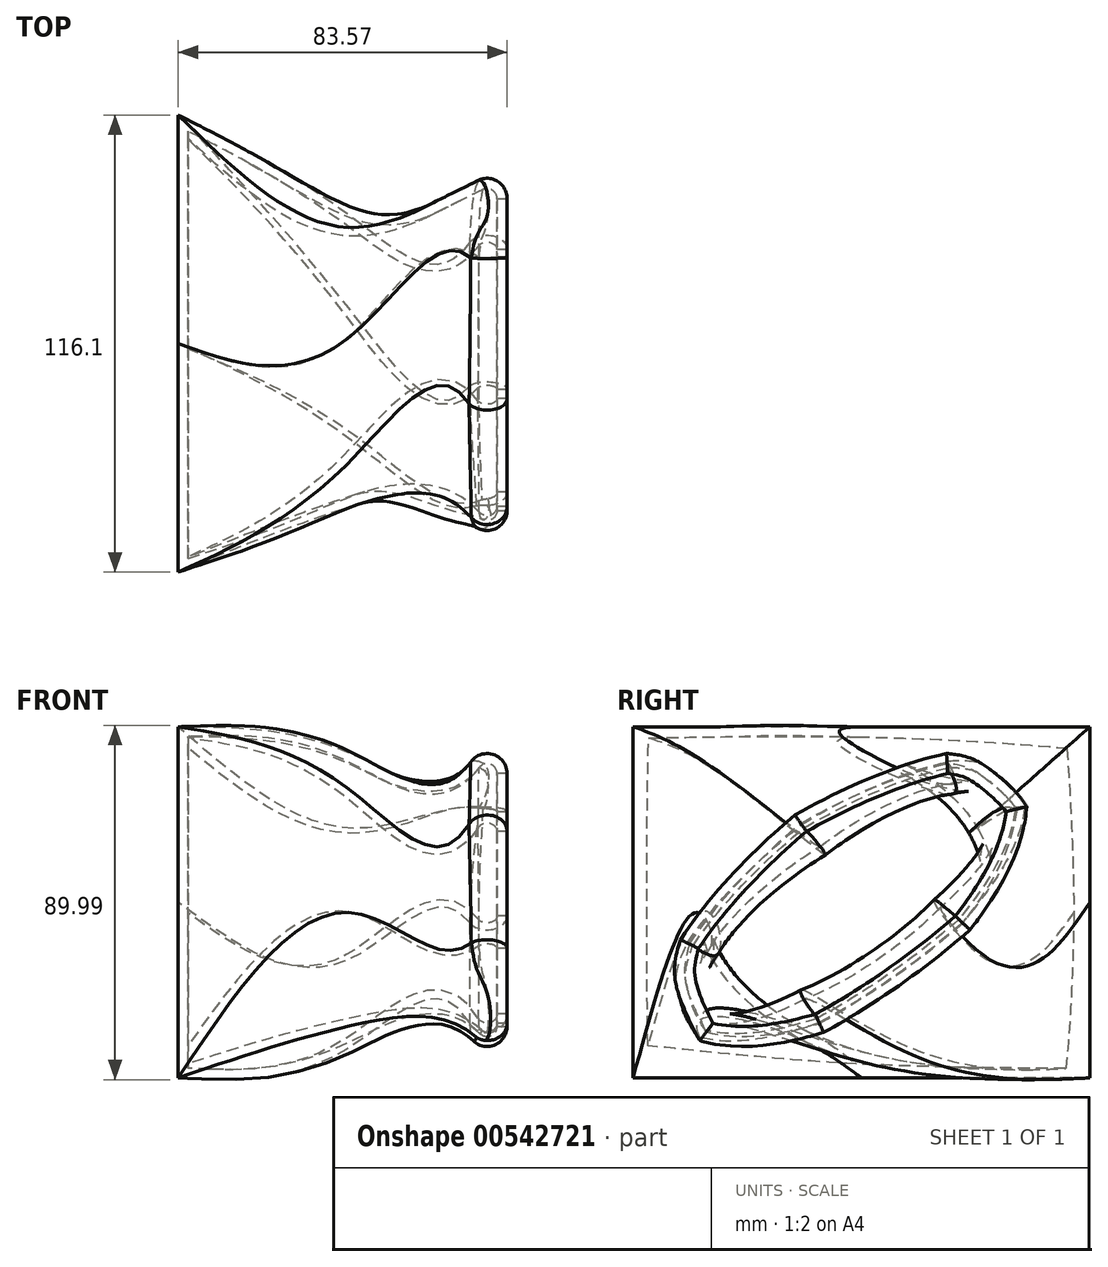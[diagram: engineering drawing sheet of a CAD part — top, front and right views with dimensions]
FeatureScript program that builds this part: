
annotation { "Feature Type Name" : "Feature", "Feature Type Description" : "" }
export const myFeature = defineFeature(function(context is Context, id is Id, definition is map)
    precondition{}
    {
        {
            var Q0;
            Q0=qCreatedBy(makeId("Right.planeOp"),FACE);
            cPlane(context, id + "F0", {"entities" : qUnion([Q0]), "cplaneType" : CPlaneType.OFFSET, "offset" : 25.4 * mm, "width" : 152.4 * mm, "height" : 152.4 * mm});
        }
        {
            var Q0;
            Q0=qCreatedBy(makeId("Right.planeOp"),FACE);
            cPlane(context, id + "F1", {"entities" : qUnion([Q0]), "cplaneType" : CPlaneType.OFFSET, "offset" : 39.12 * mm, "width" : 152.4 * mm, "height" : 152.4 * mm});
        }
        {
            var Q0;
            Q0=qCreatedBy(id+"F1.planeOp",FACE);
            var sketch = newSketch(context, id + "F2", { "sketchPlane" : qUnion([Q0])});
            skCircle(sketch, "E0.cCircle", {"center": v(0, 0) * mm, "radius": 48.41 * mm, "construction": true});
            skLineSegment(sketch, "E0.0", {"start": v(48.41, 23.32) * mm, "end": v(48.41, -23.32) * mm});
            skLineSegment(sketch, "E0.1", {"start": v(48.41, -23.32) * mm, "end": v(11.96, -52.39) * mm});
            skLineSegment(sketch, "E0.2", {"start": v(11.96, -52.39) * mm, "end": v(-33.5, -42.01) * mm});
            skLineSegment(sketch, "E0.3", {"start": v(-33.5, -42.01) * mm, "end": v(-53.74, 0) * mm});
            skLineSegment(sketch, "E0.4", {"start": v(-53.74, 0) * mm, "end": v(-33.5, 42.01) * mm});
            skLineSegment(sketch, "E0.5", {"start": v(-33.5, 42.01) * mm, "end": v(11.96, 52.39) * mm});
            skLineSegment(sketch, "E0.6", {"start": v(11.96, 52.39) * mm, "end": v(48.41, 23.32) * mm});
            skPoint(sketch, "E0.0.midPoint", {"position": v(48.41, 0) * mm});
            skSolve(sketch);
        }
        {
            var Q0;
            Q0=qCreatedBy(id+"F0.planeOp",FACE);
            var sketch = newSketch(context, id + "F3", { "sketchPlane" : qUnion([Q0])});
            skEllipse(sketch, "E1", {"center": v(0, 0) * mm, "majorRadius": 49.6 * mm, "minorRadius": 17.09 * mm, "majorAxis": v(0.82, 0.58)});
            skSolve(sketch);
        }
        {
            var Q0;
            Q0=qCreatedBy(makeId("Right.planeOp"),FACE);
            var sketch = newSketch(context, id + "F4", { "sketchPlane" : qUnion([Q0])});
            skCircle(sketch, "E2", {"center": v(0, 0) * mm, "radius": 37.91 * mm});
            skSolve(sketch);
        }
        {
            var Q0;
            Q0=qCreatedBy(makeId("Right.planeOp"),FACE);
            cPlane(context, id + "F5", {"entities" : qUnion([Q0]), "cplaneType" : CPlaneType.OFFSET, "offset" : 44.45 * mm, "oppositeDirection" : true, "width" : 152.4 * mm, "height" : 152.4 * mm});
        }
        {
            var Q0;
            Q0=qCreatedBy(id+"F5.planeOp",FACE);
            var sketch = newSketch(context, id + "F6", { "sketchPlane" : qUnion([Q0])});
            skLineSegment(sketch, "E3.bottom", {"start": v(61.49, -44.6) * mm, "end": v(-54.6, -44.6) * mm});
            skLineSegment(sketch, "E3.top", {"start": v(61.49, 44.6) * mm, "end": v(-54.6, 44.6) * mm});
            skLineSegment(sketch, "E3.left", {"start": v(61.49, -44.6) * mm, "end": v(61.49, 44.6) * mm});
            skLineSegment(sketch, "E3.right", {"start": v(-54.6, -44.6) * mm, "end": v(-54.6, 44.6) * mm});
            skPoint(sketch, "E3.middle", {"position": v(3.44, 0) * mm});
            skSolve(sketch);
        }
        {
            var Q0;
            Q0=makeQuery(id+"F2.imprint","IMPRINT",FACE,{"disambiguationData":[TD([[makeQuery(id+"F2.imprint","IMPRINT",EDGE,{"derivedFrom":sQuery(id+"F2.wireOp",EDGE,"E0.0")}),-1.0]])]});
            var Q1;
            Q1=makeQuery(id+"F3.imprint","IMPRINT",FACE,{"disambiguationData":[TD([[makeQuery(id+"F3.imprint","IMPRINT",EDGE,{"derivedFrom":sQuery(id+"F3.wireOp",EDGE,"E1")}),1.0]])]});
            var Q2;
            Q2=makeQuery(id+"F4.imprint","IMPRINT",FACE,{"disambiguationData":[TD([[makeQuery(id+"F4.imprint","IMPRINT",EDGE,{"derivedFrom":sQuery(id+"F4.wireOp",EDGE,"E2")}),1.0]])]});
            var Q3;
            Q3=makeQuery(id+"F6.imprint","IMPRINT",FACE,{"disambiguationData":[TD([[makeQuery(id+"F6.imprint","IMPRINT",EDGE,{"derivedFrom":sQuery(id+"F6.wireOp",EDGE,"E3.bottom")}),-1.0]])]});
            loft(context, id + "F7", {"sheetProfilesArray" : [{ "sheetProfileEntities" : qUnion([Q0]) }, { "sheetProfileEntities" : qUnion([Q1]) }, { "sheetProfileEntities" : qUnion([Q2]) }, { "sheetProfileEntities" : qUnion([Q3]) }]});
        }
        {
            var Q0;
            Q0=makeQuery(id+"F7.opLoft","MID_CAP_EDGE",EDGE,{"disambiguationData":[OSD([sQuery(id+"F2.wireOp",EDGE,"E0.1"),sQuery(id+"F2.wireOp",EDGE,"E0.2"),sQuery(id+"F2.wireOp",EDGE,"E0.3")])],"capPos":0.0});
            var Q1;
            Q1=makeQuery(id+"F7.opLoft","MID_CAP_EDGE",EDGE,{"disambiguationData":[OSD([sQuery(id+"F2.wireOp",EDGE,"E0.0"),sQuery(id+"F2.wireOp",EDGE,"E0.1"),sQuery(id+"F2.wireOp",EDGE,"E0.2")])],"capPos":0.0});
            var Q2;
            Q2=makeQuery(id+"F7.opLoft","MID_CAP_EDGE",EDGE,{"disambiguationData":[OSD([sQuery(id+"F2.wireOp",EDGE,"E0.0"),sQuery(id+"F2.wireOp",EDGE,"E0.1"),sQuery(id+"F2.wireOp",EDGE,"E0.6")])],"capPos":0.0});
            var Q3;
            Q3=makeQuery(id+"F7.opLoft","MID_CAP_EDGE",EDGE,{"disambiguationData":[OSD([sQuery(id+"F2.wireOp",EDGE,"E0.0"),sQuery(id+"F2.wireOp",EDGE,"E0.5"),sQuery(id+"F2.wireOp",EDGE,"E0.6")])],"capPos":0.0});
            var Q4;
            Q4=makeQuery(id+"F7.opLoft","MID_CAP_EDGE",EDGE,{"disambiguationData":[OSD([sQuery(id+"F2.wireOp",EDGE,"E0.4"),sQuery(id+"F2.wireOp",EDGE,"E0.5"),sQuery(id+"F2.wireOp",EDGE,"E0.6")])],"capPos":0.0});
            var Q5;
            Q5=makeQuery(id+"F7.opLoft","MID_CAP_EDGE",EDGE,{"disambiguationData":[OSD([sQuery(id+"F2.wireOp",EDGE,"E0.3"),sQuery(id+"F2.wireOp",EDGE,"E0.4"),sQuery(id+"F2.wireOp",EDGE,"E0.5")])],"capPos":0.0});
            var Q6;
            Q6=makeQuery(id+"F7.opLoft","MID_CAP_EDGE",EDGE,{"disambiguationData":[OSD([sQuery(id+"F2.wireOp",EDGE,"E0.2"),sQuery(id+"F2.wireOp",EDGE,"E0.3"),sQuery(id+"F2.wireOp",EDGE,"E0.4")])],"capPos":0.0});
            fillet(context, id + "F8", {"entities" : qUnion([Q0, Q1, Q2, Q3, Q4, Q5, Q6]), "radius" : 5.08 * mm, "tangentPropagation" : true, "allowEdgeOverflow" : false});
        }
        {
            var Q0;
            Q0=makeQuery(id+"F7.opLoft","CAP_FACE",FACE,{"disambiguationData":[OSD([makeQuery(id+"F2.imprint","IMPRINT",FACE,{"disambiguationData":[TD([[makeQuery(id+"F2.imprint","IMPRINT",EDGE,{"derivedFrom":sQuery(id+"F2.wireOp",EDGE,"E0.0")}),-1.0]])]})])],"isStart":true});
            shell(context, id + "F9", {"entities" : qUnion([Q0]), "thickness" : 2.54 * mm});
        }
    });
